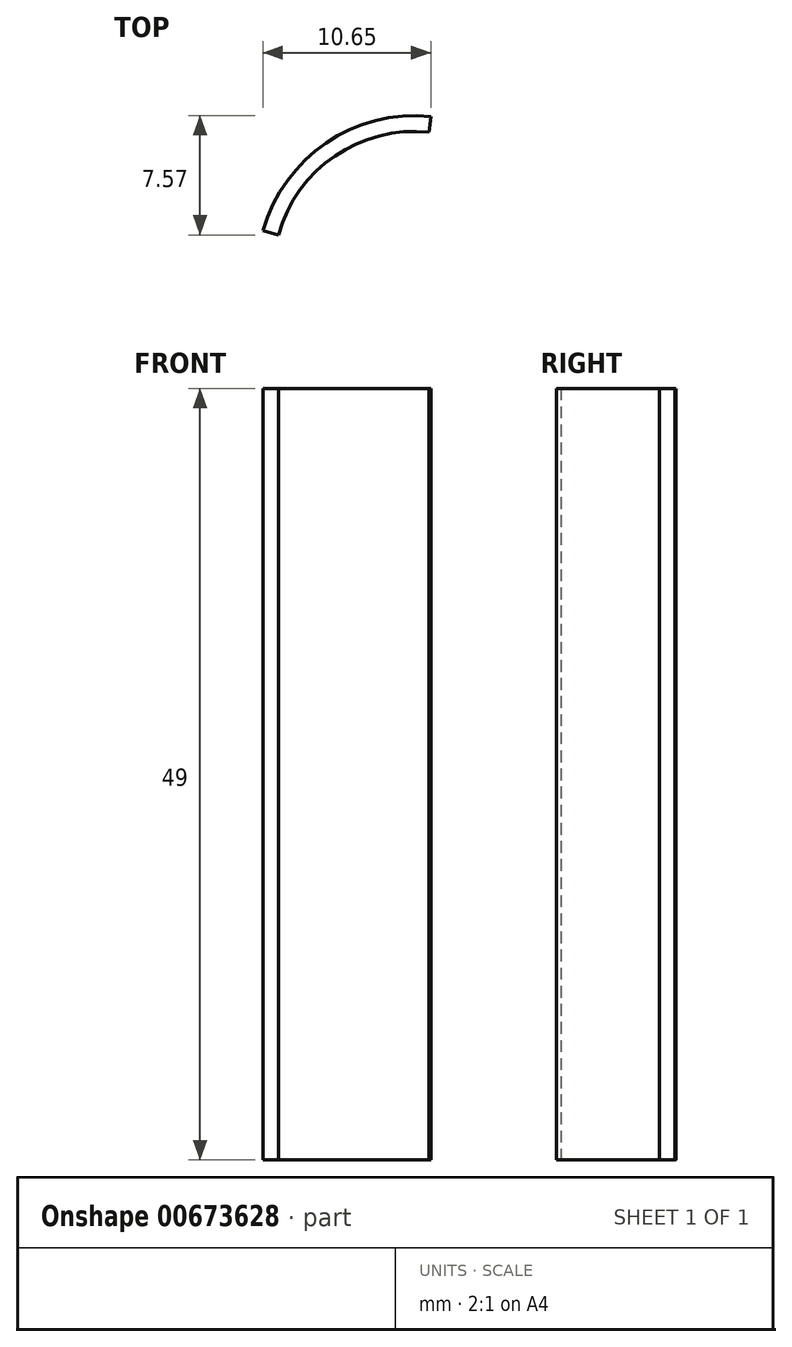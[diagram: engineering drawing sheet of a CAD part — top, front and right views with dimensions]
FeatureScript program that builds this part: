
annotation { "Feature Type Name" : "Feature", "Feature Type Description" : "" }
export const myFeature = defineFeature(function(context is Context, id is Id, definition is map)
    precondition{}
    {
        {
            var Q0;
            Q0=qCreatedBy(makeId("Top.planeOp"),FACE);
            var sketch = newSketch(context, id + "F0", { "sketchPlane" : qUnion([Q0])});
            skArc(sketch, "E0", {"start": v(0, 18.47) * mm, "mid": v(-6.65, 16.79) * mm, "end": v(-10.65, 11.21) * mm});
            skArc(sketch, "E1.0", {"start": v(-0.1, 17.48) * mm, "mid": v(-6.08, 15.96) * mm, "end": v(-9.68, 10.95) * mm});
            skLineSegment(sketch, "E2", {"start": v(-10.65, 11.21) * mm, "end": v(-9.68, 10.95) * mm});
            skLineSegment(sketch, "E3", {"start": v(0, 18.47) * mm, "end": v(-0.1, 17.48) * mm});
            skSolve(sketch);
        }
        {
            var Q0;
            Q0=makeQuery(id+"F0.imprint","IMPRINT",FACE,{"disambiguationData":[TD([[makeQuery(id+"F0.imprint","IMPRINT",EDGE,{"derivedFrom":sQuery(id+"F0.wireOp",EDGE,"E0")}),1.0]])]});
            extrude(context, id + "F1", {"entities" : qUnion([Q0]), "depth" : 49 * mm, "offsetDistance" : 25 * mm});
        }
    });
